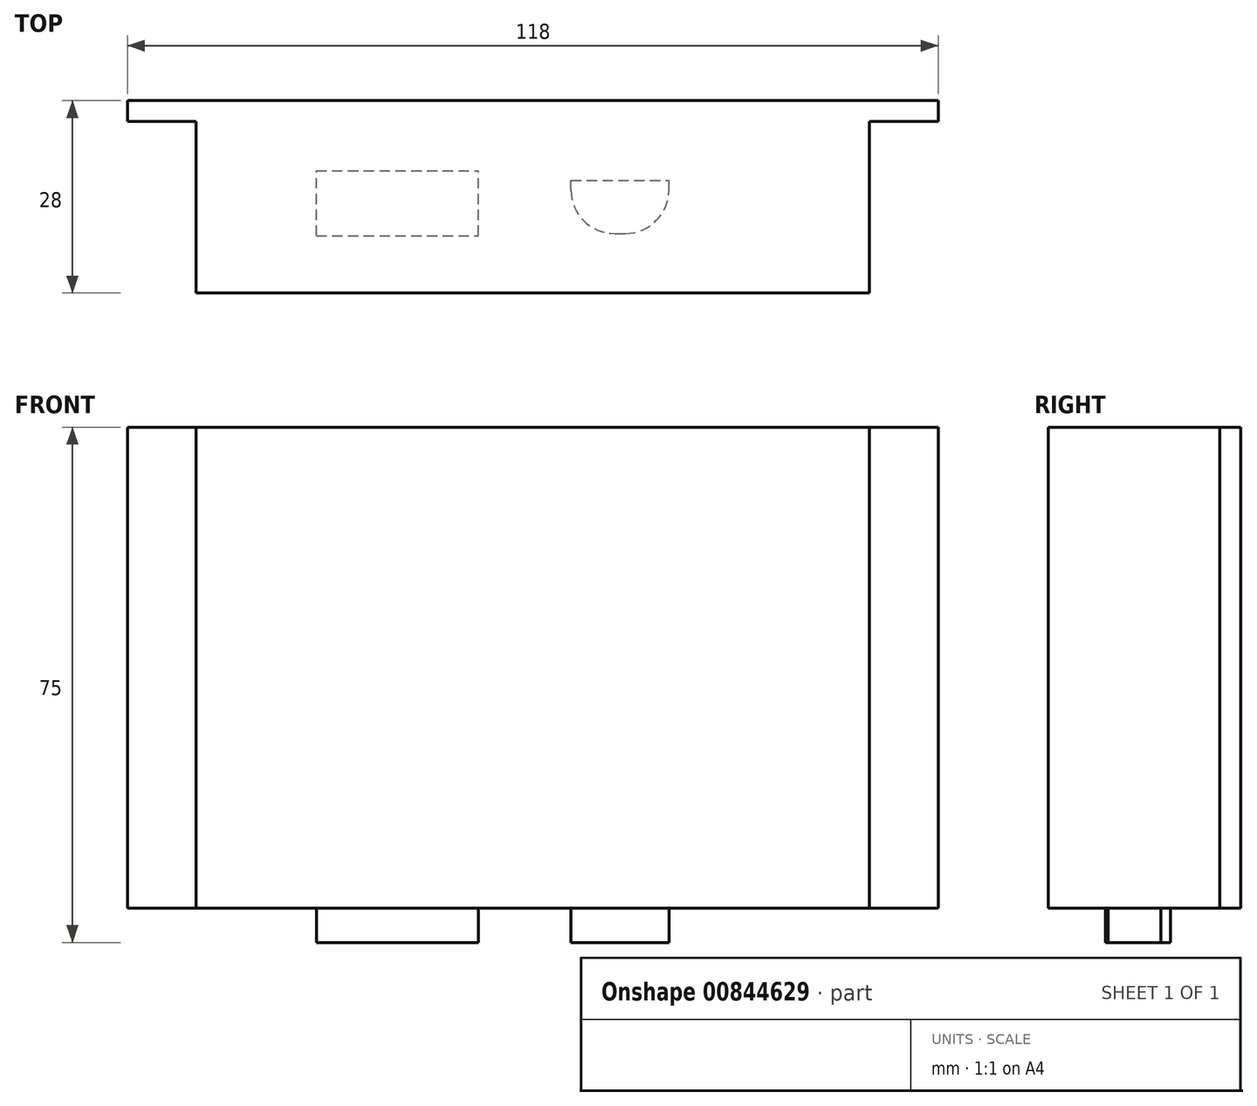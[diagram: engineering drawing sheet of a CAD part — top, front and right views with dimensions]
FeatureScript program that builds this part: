
annotation { "Feature Type Name" : "Feature", "Feature Type Description" : "" }
export const myFeature = defineFeature(function(context is Context, id is Id, definition is map)
    precondition{}
    {
        {
            var Q0;
            Q0=qCreatedBy(makeId("Front.planeOp"),FACE);
            var sketch = newSketch(context, id + "F0", { "sketchPlane" : qUnion([Q0])});
            skLineSegment(sketch, "E0.bottom", {"start": v(59, -35) * mm, "end": v(-59, -35) * mm});
            skLineSegment(sketch, "E0.top", {"start": v(59, 35) * mm, "end": v(-59, 35) * mm});
            skLineSegment(sketch, "E0.left", {"start": v(59, -35) * mm, "end": v(59, 35) * mm});
            skLineSegment(sketch, "E0.right", {"start": v(-59, -35) * mm, "end": v(-59, 35) * mm});
            skPoint(sketch, "E0.middle", {"position": v(0, 0) * mm});
            skSolve(sketch);
        }
        {
            var Q0;
            Q0=makeQuery(id+"F0.imprint","IMPRINT",FACE,{"disambiguationData":[TD([[makeQuery(id+"F0.imprint","IMPRINT",EDGE,{"derivedFrom":sQuery(id+"F0.wireOp",EDGE,"E0.bottom")}),-1.0]])]});
            extrude(context, id + "F1", {"entities" : qUnion([Q0]), "depth" : 28 * mm, "offsetDistance" : 25 * mm});
        }
        {
            var Q0;
            Q0=makeQuery(id+"F1.opExtrude","CAP_FACE",FACE,{"disambiguationData":[OSD([sQuery(id+"F0.wireOp",EDGE,"E0.bottom"),sQuery(id+"F0.wireOp",EDGE,"E0.top"),sQuery(id+"F0.wireOp",EDGE,"E0.left"),sQuery(id+"F0.wireOp",EDGE,"E0.right")])],"isStart":false});
            var sketch = newSketch(context, id + "F2", { "sketchPlane" : qUnion([Q0])});
            skLineSegment(sketch, "E1.0", {"start": v(-49, -35) * mm, "end": v(-49, 35) * mm});
            skLineSegment(sketch, "E2.0", {"start": v(49, -35) * mm, "end": v(49, 35) * mm});
            skSolve(sketch);
        }
        {
            var Q0;
            {var subQ0=sQuery(id+"F2.wireOp",EDGE,"E2.0");Q0=makeQuery(id+"F2.imprint","IMPRINT",FACE,{"disambiguationData":[TD([[makeQuery(id+"F2.imprint","IMPRINT",EDGE,{"derivedFrom":subQ0}),-1.0]])]});}
            var Q1;
            {var subQ0=sQuery(id+"F2.wireOp",EDGE,"E1.0");Q1=makeQuery(id+"F2.imprint","IMPRINT",FACE,{"disambiguationData":[TD([[makeQuery(id+"F2.imprint","IMPRINT",EDGE,{"derivedFrom":subQ0}),1.0]])]});}
            extrude(context, id + "F3", {"entities" : qUnion([Q0, Q1]), "operationType" : NewBodyOperationType.REMOVE, "oppositeDirection" : true, "depth" : 25 * mm, "offsetDistance" : 25 * mm});
        }
        {
            var Q0;
            Q0=makeQuery(id+"F1.opExtrude","SWEPT_FACE",FACE,{"disambiguationData":[OSD([sQuery(id+"F0.wireOp",EDGE,"E0.bottom")])]});
            var sketch = newSketch(context, id + "F4", { "sketchPlane" : qUnion([Q0])});
            skLineSegment(sketch, "E3.bottom", {"start": v(-31.5, 19.66) * mm, "end": v(-7.94, 19.66) * mm});
            skLineSegment(sketch, "E3.top", {"start": v(-31.5, 10.2) * mm, "end": v(-7.94, 10.2) * mm});
            skLineSegment(sketch, "E3.left", {"start": v(-31.5, 19.66) * mm, "end": v(-31.5, 10.2) * mm});
            skLineSegment(sketch, "E3.right", {"start": v(-7.94, 19.66) * mm, "end": v(-7.94, 10.2) * mm});
            skLineSegment(sketch, "E4.bottom", {"start": v(11.9, 19.32) * mm, "end": v(13.47, 19.32) * mm});
            skLineSegment(sketch, "E4.top", {"start": v(5.55, 11.6) * mm, "end": v(19.82, 11.6) * mm});
            skLineSegment(sketch, "E4.left", {"start": v(5.55, 12.97) * mm, "end": v(5.55, 11.6) * mm});
            skLineSegment(sketch, "E4.right", {"start": v(19.82, 12.97) * mm, "end": v(19.82, 11.6) * mm});
            skPoint(sketch, "E5.visualSharp", {"position": v(5.55, 19.32) * mm});
            skArc(sketch, "E5.filletArc", {"start": v(11.9, 19.32) * mm, "mid": v(7.4, 17.46) * mm, "end": v(5.55, 12.97) * mm});
            skPoint(sketch, "E6.visualSharp", {"position": v(19.82, 19.32) * mm});
            skArc(sketch, "E6.filletArc", {"start": v(19.82, 12.97) * mm, "mid": v(17.96, 17.46) * mm, "end": v(13.47, 19.32) * mm});
            skSolve(sketch);
        }
        {
            var Q0;
            Q0=makeQuery(id+"F4.imprint","IMPRINT",FACE,{"disambiguationData":[TD([[makeQuery(id+"F4.imprint","IMPRINT",EDGE,{"derivedFrom":sQuery(id+"F4.wireOp",EDGE,"E4.bottom")}),-1.0]])]});
            var Q1;
            Q1=makeQuery(id+"F4.imprint","IMPRINT",FACE,{"disambiguationData":[TD([[makeQuery(id+"F4.imprint","IMPRINT",EDGE,{"derivedFrom":sQuery(id+"F4.wireOp",EDGE,"E3.bottom")}),-1.0]])]});
            extrude(context, id + "F5", {"entities" : qUnion([Q0, Q1]), "operationType" : NewBodyOperationType.ADD, "depth" : 5 * mm, "offsetDistance" : 25 * mm});
        }
    });
